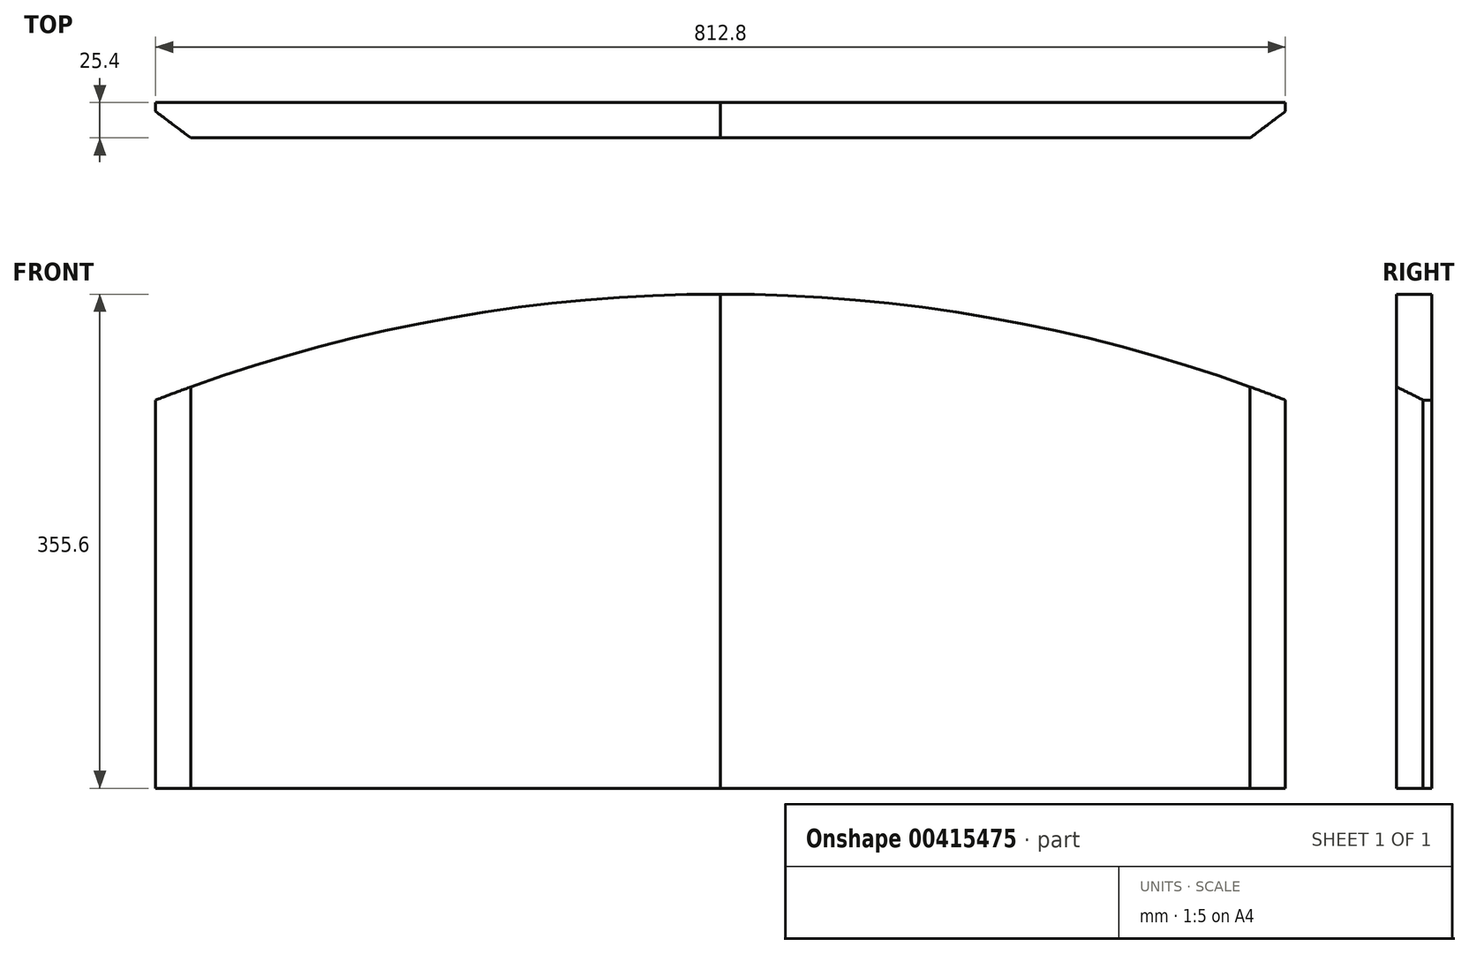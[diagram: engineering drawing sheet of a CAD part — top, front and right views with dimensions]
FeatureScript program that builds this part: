
annotation { "Feature Type Name" : "Feature", "Feature Type Description" : "" }
export const myFeature = defineFeature(function(context is Context, id is Id, definition is map)
    precondition{}
    {
        {
            var Q0;
            Q0=qCreatedBy(makeId("Front.planeOp"),FACE);
            var sketch = newSketch(context, id + "F0", { "sketchPlane" : qUnion([Q0])});
            skLineSegment(sketch, "E0.bottom", {"start": v(406.4, -139.7) * mm, "end": v(-406.4, -139.7) * mm});
            skLineSegment(sketch, "E0.left", {"start": v(406.4, -139.7) * mm, "end": v(406.4, 139.7) * mm});
            skLineSegment(sketch, "E0.right", {"start": v(-406.4, -139.7) * mm, "end": v(-406.4, 139.7) * mm});
            skPoint(sketch, "E0.middle", {"position": v(0, 0) * mm});
            skPoint(sketch, "E1", {"position": v(0, 139.7) * mm});
            skPoint(sketch, "E2", {"position": v(0, 215.9) * mm});
            skArc(sketch, "E3", {"start": v(406.4, 139.7) * mm, "mid": v(0, 215.9) * mm, "end": v(-406.4, 139.7) * mm});
            skLineSegment(sketch, "E4", {"start": v(0, 215.9) * mm, "end": v(0, -139.7) * mm});
            skSolve(sketch);
        }
        {
            var Q0;
            {var subQ0=sQuery(id+"F0.wireOp",EDGE,"E0.right");Q0=makeQuery(id+"F0.imprint","IMPRINT",FACE,{"disambiguationData":[TD([[makeQuery(id+"F0.imprint","IMPRINT",EDGE,{"derivedFrom":subQ0}),-1.0]])]});}
            extrude(context, id + "F1", {"entities" : qUnion([Q0]), "depth" : 25.4 * mm});
        }
        {
            var Q0;
            {var subQ0=sQuery(id+"F0.wireOp",EDGE,"E0.left");Q0=makeQuery(id+"F0.imprint","IMPRINT",FACE,{"disambiguationData":[TD([[makeQuery(id+"F0.imprint","IMPRINT",EDGE,{"derivedFrom":subQ0}),1.0]])]});}
            extrude(context, id + "F2", {"entities" : qUnion([Q0]), "depth" : 25.4 * mm});
        }
        {
            var Q0;
            Q0=makeQuery(id+"F1.opExtrude","CAP_EDGE",EDGE,{"disambiguationData":[OSD([sQuery(id+"F0.wireOp",EDGE,"E0.right")])],"isStart":false});
            chamfer(context, id + "F3", {"entities" : qUnion([Q0]), "chamferType" : ChamferType.TWO_OFFSETS, "width1" : 19.05 * mm, "oppositeDirection" : false, "width2" : 25.4 * mm, "tangentPropagation" : true});
        }
        {
            var Q0;
            Q0=makeQuery(id+"F2.opExtrude","CAP_EDGE",EDGE,{"disambiguationData":[OSD([sQuery(id+"F0.wireOp",EDGE,"E0.left")])],"isStart":false});
            chamfer(context, id + "F4", {"entities" : qUnion([Q0]), "chamferType" : ChamferType.TWO_OFFSETS, "width1" : 25.4 * mm, "oppositeDirection" : false, "width2" : 19.05 * mm, "tangentPropagation" : true});
        }
    });
